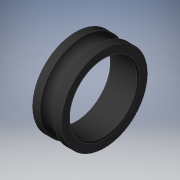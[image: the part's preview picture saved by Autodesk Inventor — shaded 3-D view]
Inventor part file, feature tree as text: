
AUTODESK INVENTOR PART (.ipt)
format: ipt  version: 2019 (Build 230136000, 136)  size: 167,936 bytes
history: native  units: mm
features: other x7, revolve x1, sketch x1
ambient origin geometry x8: Origin, YZ Plane, XZ Plane, XY Plane, X Axis, Y Axis, Z Axis, Center Point
bodies: Solid1 (feature_tree)
feature tree (9):
  revolve  "Revolution1"  [1 undecoded]
  other  "dgbb_ir_XY"
  other  "dgbb_ir_YZ"
  other  "dgbb_ir_ZX"
  other  "dgbb_ir_X"
  other  "dgbb_ir_Y"
  other  "dgbb_ir_Z"
  other  "dgbb_ir_Center"
  sketch  "Sketch_1"  dims[d0=360.0deg d1=0.0mm]
note: 1 required parameter value undecoded (feature->parameter linkage not recoverable at this tier; creation-order binding heuristic only, values carry confidence <= 0.55)
